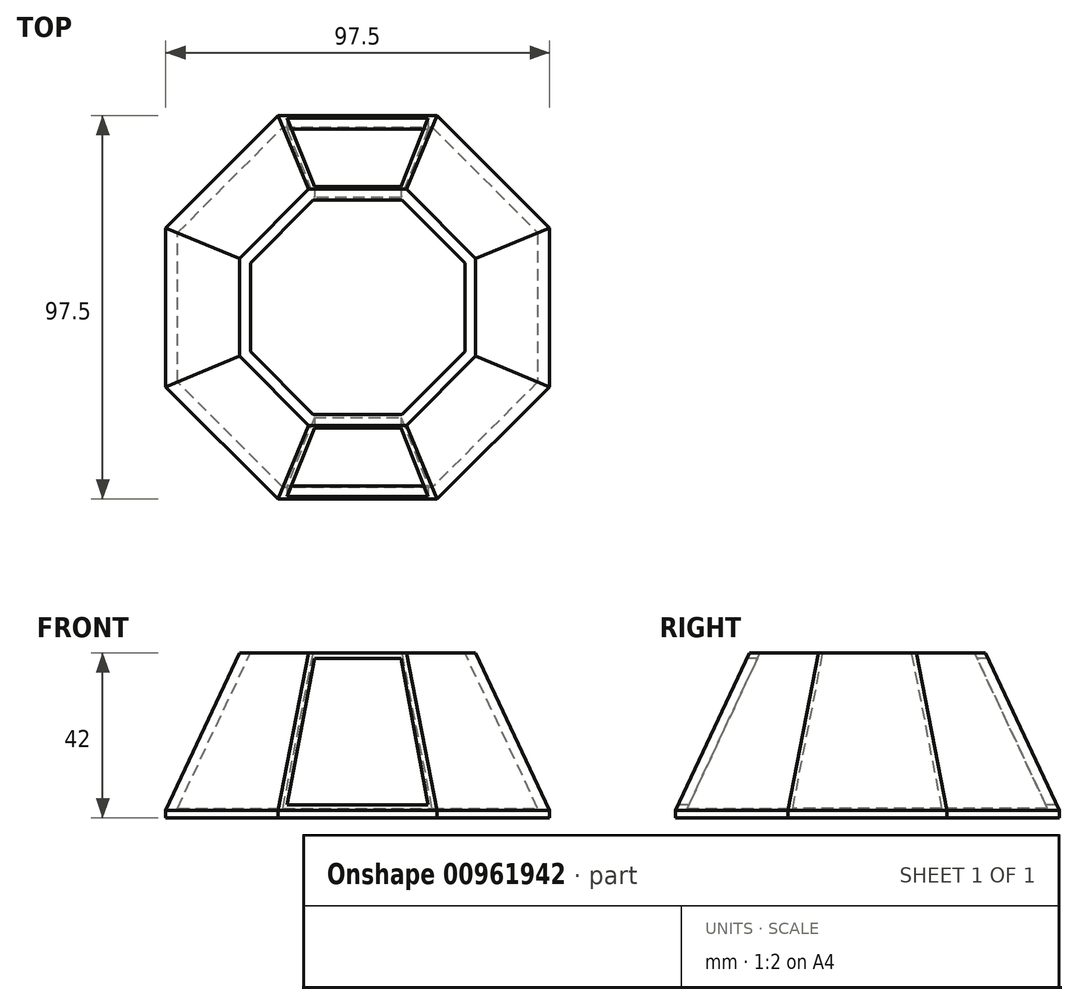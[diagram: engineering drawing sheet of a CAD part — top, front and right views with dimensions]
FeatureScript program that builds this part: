
annotation { "Feature Type Name" : "Feature", "Feature Type Description" : "" }
export const myFeature = defineFeature(function(context is Context, id is Id, definition is map)
    precondition{}
    {
        {
            var Q0;
            Q0=qCreatedBy(makeId("Top.planeOp"),FACE);
            var sketch = newSketch(context, id + "F0", { "sketchPlane" : qUnion([Q0])});
            skCircle(sketch, "E0", {"center": v(0, 0) * mm, "radius": 48.75 * mm});
            skCircle(sketch, "E1.cCircle", {"center": v(0, 0) * mm, "radius": 48.75 * mm, "construction": true});
            skLineSegment(sketch, "E1.0", {"start": v(-48.75, -20.2) * mm, "end": v(-48.75, 20.2) * mm});
            skLineSegment(sketch, "E1.1", {"start": v(-48.75, 20.2) * mm, "end": v(-20.2, 48.75) * mm});
            skLineSegment(sketch, "E1.2", {"start": v(-20.2, 48.75) * mm, "end": v(20.2, 48.75) * mm});
            skLineSegment(sketch, "E1.3", {"start": v(20.2, 48.75) * mm, "end": v(48.75, 20.2) * mm});
            skLineSegment(sketch, "E1.4", {"start": v(48.75, 20.2) * mm, "end": v(48.75, -20.2) * mm});
            skLineSegment(sketch, "E1.5", {"start": v(48.75, -20.2) * mm, "end": v(20.2, -48.75) * mm});
            skLineSegment(sketch, "E1.6", {"start": v(20.2, -48.75) * mm, "end": v(-20.2, -48.75) * mm});
            skLineSegment(sketch, "E1.7", {"start": v(-20.2, -48.75) * mm, "end": v(-48.75, -20.2) * mm});
            skPoint(sketch, "E1.0.midPoint", {"position": v(-48.75, 0) * mm});
            skSolve(sketch);
        }
        {
            var Q0;
            Q0=qSketchRegion(id+"F0",true);
            extrude(context, id + "F1", {"entities" : qUnion([Q0]), "depth" : 2 * mm, "offsetDistance" : 25 * mm});
        }
        {
            var Q0;
            Q0=makeQuery(id+"F1.opExtrude","CAP_FACE",FACE,{"disambiguationData":[OSD([sQuery(id+"F0.wireOp",EDGE,"E1.0"),sQuery(id+"F0.wireOp",EDGE,"E1.1"),sQuery(id+"F0.wireOp",EDGE,"E1.2"),sQuery(id+"F0.wireOp",EDGE,"E1.3"),sQuery(id+"F0.wireOp",EDGE,"E1.4"),sQuery(id+"F0.wireOp",EDGE,"E1.5"),sQuery(id+"F0.wireOp",EDGE,"E1.6"),sQuery(id+"F0.wireOp",EDGE,"E1.7")])],"isStart":false});
            cPlane(context, id + "F2", {"entities" : qUnion([Q0]), "cplaneType" : CPlaneType.OFFSET, "offset" : 40 * mm, "width" : 150 * mm, "height" : 150 * mm});
        }
        {
            var Q0;
            Q0=qCreatedBy(id+"F2.planeOp",FACE);
            var sketch = newSketch(context, id + "F3", { "sketchPlane" : qUnion([Q0])});
            skLineSegment(sketch, "E2.0", {"start": v(-30, -12.43) * mm, "end": v(-30, 12.43) * mm});
            skLineSegment(sketch, "E2.1", {"start": v(-30, 12.43) * mm, "end": v(-12.43, 30) * mm});
            skLineSegment(sketch, "E2.2", {"start": v(-12.43, 30) * mm, "end": v(12.43, 30) * mm});
            skLineSegment(sketch, "E2.3", {"start": v(12.43, 30) * mm, "end": v(30, 12.43) * mm});
            skLineSegment(sketch, "E2.4", {"start": v(30, 12.43) * mm, "end": v(30, -12.43) * mm});
            skLineSegment(sketch, "E2.5", {"start": v(30, -12.43) * mm, "end": v(12.43, -30) * mm});
            skLineSegment(sketch, "E2.6", {"start": v(12.43, -30) * mm, "end": v(-12.43, -30) * mm});
            skLineSegment(sketch, "E2.7", {"start": v(-12.43, -30) * mm, "end": v(-30, -12.43) * mm});
            skPoint(sketch, "E2.0.midPoint", {"position": v(-30, 0) * mm});
            skSolve(sketch);
        }
        {
            var Q0;
            Q0=makeQuery(id+"F1.opExtrude","CAP_FACE",FACE,{"disambiguationData":[OSD([sQuery(id+"F0.wireOp",EDGE,"E1.0"),sQuery(id+"F0.wireOp",EDGE,"E1.1"),sQuery(id+"F0.wireOp",EDGE,"E1.2"),sQuery(id+"F0.wireOp",EDGE,"E1.3"),sQuery(id+"F0.wireOp",EDGE,"E1.4"),sQuery(id+"F0.wireOp",EDGE,"E1.5"),sQuery(id+"F0.wireOp",EDGE,"E1.6"),sQuery(id+"F0.wireOp",EDGE,"E1.7")])],"isStart":false});
            var sketch = newSketch(context, id + "F4", { "sketchPlane" : qUnion([Q0])});
            skCircle(sketch, "E3.cCircle", {"center": v(0, 0) * mm, "radius": 48.75 * mm, "construction": true});
            skLineSegment(sketch, "E3.0", {"start": v(-48.75, -20.2) * mm, "end": v(-48.75, 20.2) * mm});
            skLineSegment(sketch, "E3.1", {"start": v(-48.75, 20.2) * mm, "end": v(-20.2, 48.75) * mm});
            skLineSegment(sketch, "E3.2", {"start": v(-20.2, 48.75) * mm, "end": v(20.2, 48.75) * mm});
            skLineSegment(sketch, "E3.3", {"start": v(20.2, 48.75) * mm, "end": v(48.75, 20.2) * mm});
            skLineSegment(sketch, "E3.4", {"start": v(48.75, 20.2) * mm, "end": v(48.75, -20.2) * mm});
            skLineSegment(sketch, "E3.5", {"start": v(48.75, -20.2) * mm, "end": v(20.2, -48.75) * mm});
            skLineSegment(sketch, "E3.6", {"start": v(20.2, -48.75) * mm, "end": v(-20.2, -48.75) * mm});
            skLineSegment(sketch, "E3.7", {"start": v(-20.2, -48.75) * mm, "end": v(-48.75, -20.2) * mm});
            skPoint(sketch, "E3.0.midPoint", {"position": v(-48.75, 0) * mm});
            skSolve(sketch);
        }
        {
            var Q1;
            Q1=qSketchRegion(id+"F4",true);
            var Q2;
            Q2=qSketchRegion(id+"F3",true);
            loft(context, id + "F5", {"operationType" : NewBodyOperationType.ADD, "sheetProfilesArray" : [{ "sheetProfileEntities" : qUnion([Q1]) }, { "sheetProfileEntities" : qUnion([Q2]) }]});
        }
        {
            var Q0;
            Q0=makeQuery(id+"F5.opLoft","CAP_FACE",FACE,{"disambiguationData":[OSD([makeQuery(id+"F3.imprint","IMPRINT",FACE,{"disambiguationData":[TD([[makeQuery(id+"F3.imprint","IMPRINT",EDGE,{"derivedFrom":sQuery(id+"F3.wireOp",EDGE,"E2.0")}),-1.0]])]})])],"isStart":true});
            shell(context, id + "F6", {"entities" : qUnion([Q0]), "thickness" : 2.5 * mm});
        }
        {
            var Q0;
            Q0=qCreatedBy(makeId("Front.planeOp"),FACE);
            var sketch = newSketch(context, id + "F7", { "sketchPlane" : qUnion([Q0])});
            skLineSegment(sketch, "E4", {"start": v(17.94, 3.4) * mm, "end": v(11, 40.5) * mm});
            skLineSegment(sketch, "E5", {"start": v(11, 40.5) * mm, "end": v(0, 40.5) * mm});
            skLineSegment(sketch, "E6", {"start": v(0, 40.5) * mm, "end": v(0, 10.76) * mm});
            skLineSegment(sketch, "E7", {"start": v(17.94, 3.4) * mm, "end": v(0, 3.4) * mm});
            skLineSegment(sketch, "E8.MirrorCS", {"start": v(-11, 40.5) * mm, "end": v(0, 40.5) * mm});
            skLineSegment(sketch, "E9.MirrorCS", {"start": v(-17.94, 3.4) * mm, "end": v(-11, 40.5) * mm});
            skLineSegment(sketch, "E10.MirrorCS", {"start": v(-17.94, 3.4) * mm, "end": v(0, 3.4) * mm});
            skSolve(sketch);
        }
        {
            var Q0;
            Q0 = qSketchRegion(id + "F7", true);
            extrude(context, id + "F8", {"entities" : qUnion([Q0]), "operationType" : NewBodyOperationType.REMOVE, "endBound" : BoundingType.SYMMETRIC, "oppositeDirection" : true, "depth" : 169.6 * mm, "offsetDistance" : 25 * mm});
        }
    });
